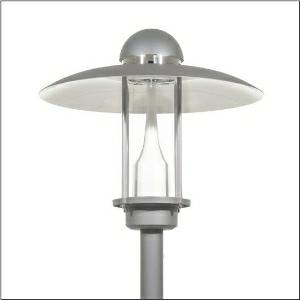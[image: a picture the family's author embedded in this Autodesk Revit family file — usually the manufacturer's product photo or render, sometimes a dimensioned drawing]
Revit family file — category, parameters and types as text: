
# Revit family: city-light_elegance_iq___pl1_2s_5xa5265jf14h_a7e3
name_source: partatom
category: Lighting Fixtures
units: mm (PartAtom-declared; Revit-internal decimal feet)

## family parameters
Cut with Voids When Loaded = No
Host = Face
Light Source = No
Part Type = Normal
Room Calculation Point = No
Round Connector Dimension = Use Diameter
Shared = No

## types (1)
- --- (1 x LED, 2840 lm, 19.3 W, 3000K)
    Apparent Load = 19 VA
    CIE Flux Codes = 24 63 94 98 100
    Color Rendering = 70
    Color Temperature = 3000K
    Default Elevation = 1800 mm
    Description = City-Light Elegance iQ, mast luminaire, Module 540 iQ-SR, primary light control with 3 zone facetted reflector, of plastic, silver coated, highly specular, structured, primary optical cover: cover, of PMMA, transparent, light distribution: PL1.2s, light emission: direct distribution, primary light characteristic: symmetric, installation type: post-top, LED, High Power LED, rated luminous flux: 2.840lm, luminous efficacy: 147lm/W, light colour: 730, colour temperature: 3000K, control gear: iQ Street-Remote, control: Auto-Match, Temp-Guard, Lumen-Switch, Night-Set, Smart-Wire, Light-Fading, Desk-Remote (wireless, voltage-free reading and setting of iQ features in the workshop via application-optimized NFC function/RFID function), optimised constant luminous flux control (CLO 2.0), Street-Remote, pre-setting: logarithmic dimming characteristic, with terminal, 6-pole, max. 2.5mm², mains connection: 230..240V, AC, 50/60Hz, start of lifetime: 19W, end of service life: 21W, reduction: 10W, luminaire housing, upper part, of aluminium, coated, Siteco® metallic grey (DB 702S), diameter: 750mm, height: 675mm, spigot size: d x l = 76 x 70mm (post-top) | with reducer (optional accessory) 60 x 70mm, mounting height: 3..5m, post-top mast mounting element, of diecast aluminium, coated, Siteco® metallic grey (DB 702S), Module 540 iQ-SR, traffic white (RAL 9016), equipment: standard, protection rating (complete): IP65, insulation class (complete): insulation class II (safety insulation), certification: CE, ENEC, VDE, packaging unit: 1 piece

Light Distribution: PL1.2s
    Height = 675 mm
    Lamp = 1 x LED
    Lamp Light Flux = 2840 lm
    Lamp Power = 19.3 W
    Lamp count = 1
    Length = 750 mm
    Luminous efficacy = 147 lm/W
    Manufacturer = Siteco
    ModVariant = No
    Model = 5XA5265JF14H
    Number of Poles = 1
    OnlyDefault = Yes
    Power Factor = 1
    Product Name = City-Light Elegance iQ | PL1.2s
    Product group = mast luminaire | pylon top
    ProductGroupID = 6100
    Protection Class = Protection class II
    Protection Degree = IP 65
    RLX_Detail_Level = 1
    RLX_Emergency_Light_Flux = 0 lm
    RLX_Emergency_Type = 0
    RLX_Emergency_Type_DB = No
    RlxData = <blob elided: 33601 chars, md5=f82e2eb3>
    Socket = socket
    Standby Power = 0 W
    System Light Flux = 2840 lm
    System Power = 19 W
    Type Comments = factory setting: luminous flux: 100 % | dim-lin: 254 | 403 mA
    Type Image = l_1006912.jpg
    URL = http://relux.com
    VarID = @adj_166855
    Voltage = 0 V
    Weight = 0.00 kg
    Width = 0 mm  [stored 0 ft]

note: [stored X ft] marks values corroborated as IEEE doubles in the binary element streams (Revit-internal decimal feet)

## geometry (parser evidence)
native form markers: Blend x4, Sweep x11
no freeform markers — native parametric forms only
